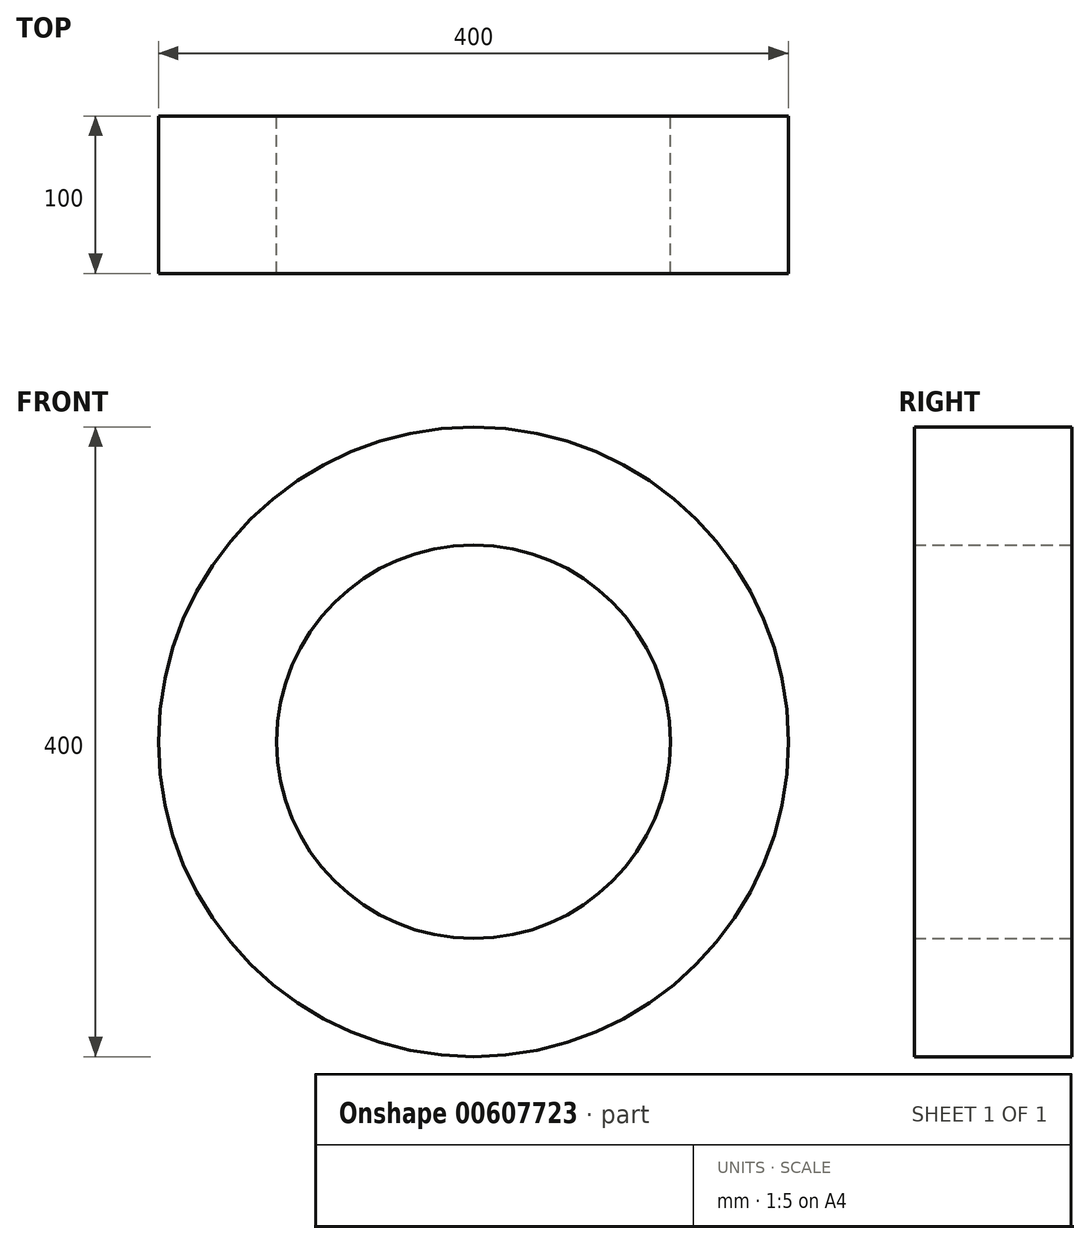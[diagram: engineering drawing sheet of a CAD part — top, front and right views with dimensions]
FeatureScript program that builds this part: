
annotation { "Feature Type Name" : "Feature", "Feature Type Description" : "" }
export const myFeature = defineFeature(function(context is Context, id is Id, definition is map)
    precondition{}
    {
        {
            var Q0;
            Q0=qCreatedBy(makeId("Front.planeOp"),FACE);
            var sketch = newSketch(context, id + "F0", { "sketchPlane" : qUnion([Q0])});
            skCircle(sketch, "E0", {"center": v(0, 0) * mm, "radius": 125 * mm});
            skSolve(sketch);
        }
        {
            var Q0;
            Q0=makeQuery(id+"F0.imprint","IMPRINT",FACE,{"disambiguationData":[TD([[makeQuery(id+"F0.imprint","IMPRINT",EDGE,{"derivedFrom":sQuery(id+"F0.wireOp",EDGE,"E0")}),1.0]])]});
            var sketch = newSketch(context, id + "F1", { "sketchPlane" : qUnion([Q0])});
            skCircle(sketch, "E1", {"center": v(0, 0) * mm, "radius": 200 * mm});
            skSolve(sketch);
        }
        {
            var Q0;
            Q0=makeQuery(id+"F0.imprint","IMPRINT",FACE,{"disambiguationData":[TD([[makeQuery(id+"F0.imprint","IMPRINT",EDGE,{"derivedFrom":sQuery(id+"F0.wireOp",EDGE,"E0")}),1.0]])]});
            var sketch = newSketch(context, id + "F2", { "sketchPlane" : qUnion([Q0])});
            skLineSegment(sketch, "E2", {"start": v(-269.4, 25) * mm, "end": v(1516.01, 25) * mm, "construction": true});
            skLineSegment(sketch, "E3", {"start": v(-260.73, 125) * mm, "end": v(1162.21, 125) * mm, "construction": true});
            skLineSegment(sketch, "E4", {"start": v(199.5, -29) * mm, "end": v(1621.37, -29) * mm});
            skSolve(sketch);
        }
        {
            var Q0;
            Q0=makeQuery(id+"F0.imprint","IMPRINT",FACE,{"disambiguationData":[TD([[makeQuery(id+"F0.imprint","IMPRINT",EDGE,{"derivedFrom":sQuery(id+"F0.wireOp",EDGE,"E0")}),1.0]])]});
            var sketch = newSketch(context, id + "F3", { "sketchPlane" : qUnion([Q0])});
            skLineSegment(sketch, "E5.bottom", {"start": v(1021.37, -29) * mm, "end": v(1621.37, -29) * mm});
            skLineSegment(sketch, "E5.top", {"start": v(1021.37, 121) * mm, "end": v(1621.37, 121) * mm});
            skLineSegment(sketch, "E5.left", {"start": v(1021.37, -29) * mm, "end": v(1021.37, 121) * mm});
            skLineSegment(sketch, "E5.right", {"start": v(1621.37, -29) * mm, "end": v(1621.37, 121) * mm});
            skSolve(sketch);
        }
        {
            var Q0;
            Q0=makeQuery(id+"F0.imprint","IMPRINT",FACE,{"disambiguationData":[TD([[makeQuery(id+"F0.imprint","IMPRINT",EDGE,{"derivedFrom":sQuery(id+"F0.wireOp",EDGE,"E0")}),1.0]])]});
            var sketch = newSketch(context, id + "F4", { "sketchPlane" : qUnion([Q0])});
            skLineSegment(sketch, "E6.bottom", {"start": v(197.89, -29) * mm, "end": v(1021.37, -29) * mm});
            skLineSegment(sketch, "E6.top", {"start": v(195.75, 41) * mm, "end": v(1021.37, 41) * mm});
            skLineSegment(sketch, "E6.right", {"start": v(1021.37, -29) * mm, "end": v(1021.37, 41) * mm});
            skSolve(sketch);
        }
        {
            var Q0;
            Q0=makeQuery(id+"F1.imprint","IMPRINT",FACE,{"disambiguationData":[TD([[makeQuery(id+"F1.imprint","IMPRINT",EDGE,{"derivedFrom":sQuery(id+"F1.wireOp",EDGE,"E1")}),1.0]])]});
            var sketch = newSketch(context, id + "F5", { "sketchPlane" : qUnion([Q0])});
            skSolve(sketch);
        }
        {
            var Q0;
            Q0=makeQuery(id+"F1.imprint","IMPRINT",FACE,{"disambiguationData":[TD([[makeQuery(id+"F1.imprint","IMPRINT",EDGE,{"derivedFrom":sQuery(id+"F1.wireOp",EDGE,"E1")}),1.0]])]});
            var sketch = newSketch(context, id + "F6", { "sketchPlane" : qUnion([Q0])});
            skSolve(sketch);
        }
        {
            var Q0;
            Q0=makeQuery(id+"F6.imprint","IMPRINT",FACE,{"disambiguationData":[TD([[makeQuery(id+"F6.imprint","IMPRINT",EDGE,{"derivedFrom":makeQuery(id+"F1.imprint","IMPRINT",EDGE,{"derivedFrom":sQuery(id+"F1.wireOp",EDGE,"E1")})}),1.0]])]});
            var Q1;
            Q1=makeQuery(id+"F0.imprint","IMPRINT",FACE,{"disambiguationData":[TD([[makeQuery(id+"F0.imprint","IMPRINT",EDGE,{"derivedFrom":sQuery(id+"F0.wireOp",EDGE,"E0")}),1.0]])]});
            var Q2;
            Q2=makeQuery(id+"F6.imprint","IMPRINT",FACE,{"disambiguationData":[TD([[makeQuery(id+"F6.imprint","IMPRINT",EDGE,{"derivedFrom":makeQuery(id+"F1.imprint","IMPRINT",EDGE,{"derivedFrom":makeQuery(id+"F0.imprint","IMPRINT",EDGE,{"derivedFrom":sQuery(id+"F0.wireOp",EDGE,"E0")})})}),1.0]])]});
            var Q3;
            Q3=makeQuery(id+"F5.imprint","IMPRINT",FACE,{"disambiguationData":[TD([[makeQuery(id+"F5.imprint","IMPRINT",EDGE,{"derivedFrom":makeQuery(id+"F1.imprint","IMPRINT",EDGE,{"derivedFrom":sQuery(id+"F1.wireOp",EDGE,"E1")})}),1.0]])]});
            var Q4;
            Q4=makeQuery(id+"F2.imprint","IMPRINT",FACE,{"disambiguationData":[TD([[makeQuery(id+"F2.imprint","IMPRINT",EDGE,{"derivedFrom":makeQuery(id+"F0.imprint","IMPRINT",EDGE,{"derivedFrom":sQuery(id+"F0.wireOp",EDGE,"E0")})}),1.0]])]});
            var Q5;
            Q5=makeQuery(id+"F1.imprint","IMPRINT",FACE,{"disambiguationData":[TD([[makeQuery(id+"F1.imprint","IMPRINT",EDGE,{"derivedFrom":sQuery(id+"F1.wireOp",EDGE,"E1")}),1.0]])]});
            var Q6;
            Q6=makeQuery(id+"F3.imprint","IMPRINT",FACE,{"disambiguationData":[TD([[makeQuery(id+"F3.imprint","IMPRINT",EDGE,{"derivedFrom":makeQuery(id+"F0.imprint","IMPRINT",EDGE,{"derivedFrom":sQuery(id+"F0.wireOp",EDGE,"E0")})}),1.0]])]});
            var Q7;
            Q7=makeQuery(id+"F4.imprint","IMPRINT",FACE,{"disambiguationData":[TD([[makeQuery(id+"F4.imprint","IMPRINT",EDGE,{"derivedFrom":makeQuery(id+"F0.imprint","IMPRINT",EDGE,{"derivedFrom":sQuery(id+"F0.wireOp",EDGE,"E0")})}),1.0]])]});
            var Q8;
            Q8=makeQuery(id+"F5.imprint","IMPRINT",FACE,{"disambiguationData":[TD([[makeQuery(id+"F5.imprint","IMPRINT",EDGE,{"derivedFrom":makeQuery(id+"F1.imprint","IMPRINT",EDGE,{"derivedFrom":makeQuery(id+"F0.imprint","IMPRINT",EDGE,{"derivedFrom":sQuery(id+"F0.wireOp",EDGE,"E0")})})}),1.0]])]});
            var Q9;
            Q9=makeQuery(id+"F1.imprint","IMPRINT",FACE,{"disambiguationData":[TD([[makeQuery(id+"F1.imprint","IMPRINT",EDGE,{"derivedFrom":makeQuery(id+"F0.imprint","IMPRINT",EDGE,{"derivedFrom":sQuery(id+"F0.wireOp",EDGE,"E0")})}),1.0]])]});
            extrude(context, id + "F7", {"entities" : qUnion([Q0, Q1, Q2, Q3, Q4, Q5, Q6, Q7, Q8, Q9]), "endBound" : BoundingType.SYMMETRIC, "depth" : 100 * mm, "offsetDistance" : 25 * mm});
        }
    });
